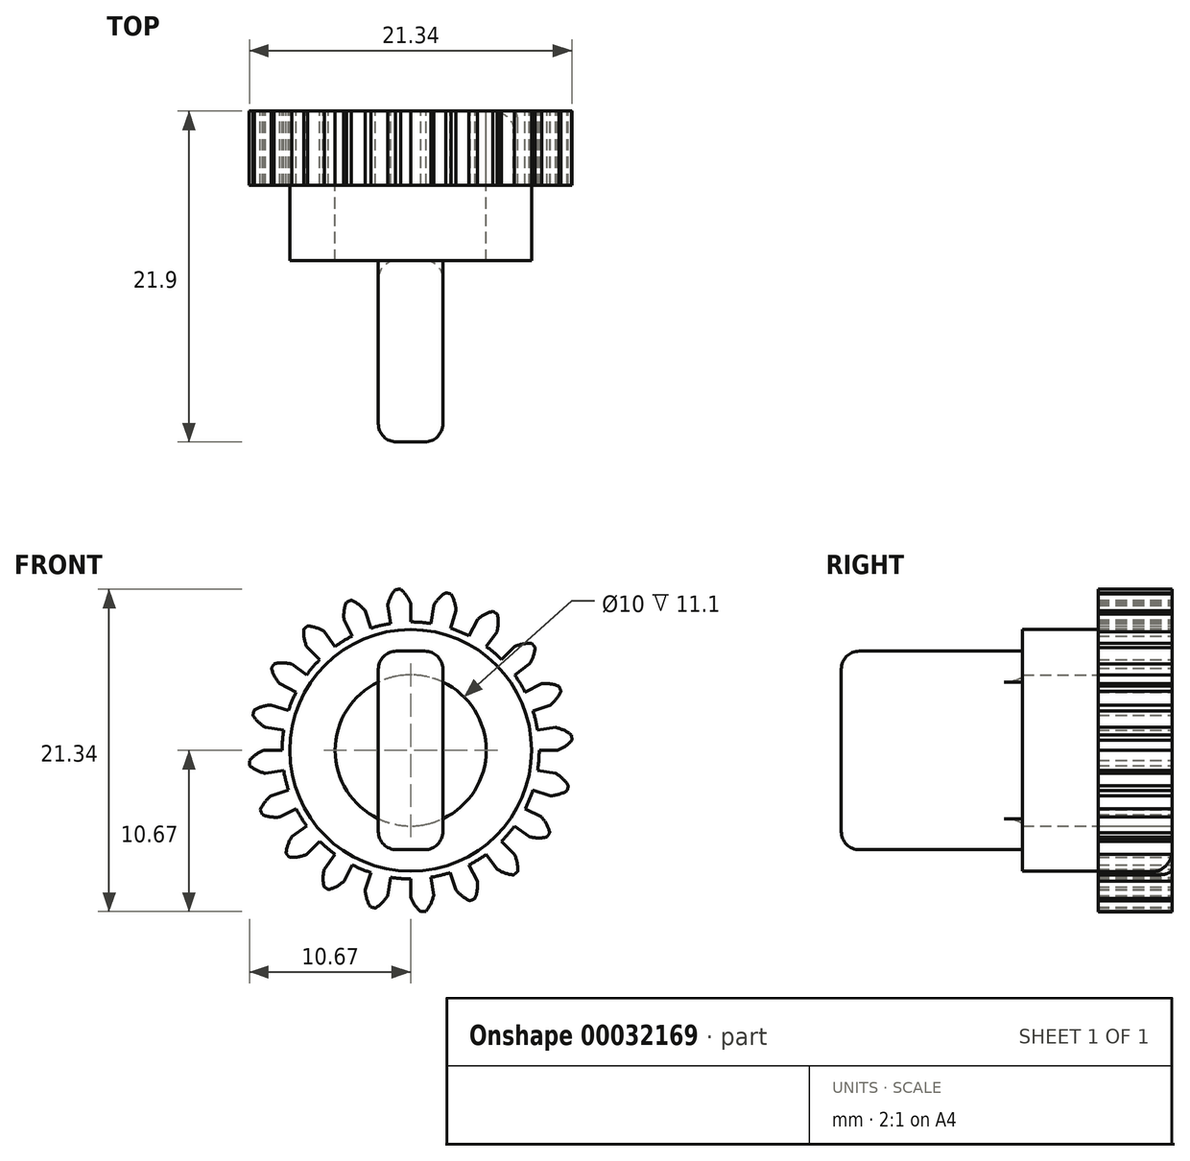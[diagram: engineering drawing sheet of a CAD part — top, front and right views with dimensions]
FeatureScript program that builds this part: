
annotation { "Feature Type Name" : "Feature", "Feature Type Description" : "" }
export const myFeature = defineFeature(function(context is Context, id is Id, definition is map)
    precondition{}
    {
        {
            var Q0;
            Q0=qCreatedBy(makeId("Front.planeOp"),FACE);
            var sketch = newSketch(context, id + "F0", { "sketchPlane" : qUnion([Q0])});
            skCircle(sketch, "E0", {"center": v(0, 0) * mm, "radius": 5 * mm});
            skArc(sketch, "E1", {"start": v(-1.33, 8.4) * mm, "mid": v(0.67, -8.48) * mm, "end": v(0, 8.5) * mm});
            skArc(sketch, "E2", {"start": v(-0.66, 10.67) * mm, "mid": v(-0.84, 10.66) * mm, "end": v(-1.01, 10.65) * mm});
            skArc(sketch, "E3.trimOffspring", {"start": v(0, 9.72) * mm, "mid": v(-0.27, 10.24) * mm, "end": v(-0.66, 10.67) * mm});
            skArc(sketch, "E4.0.MirrorCS", {"start": v(-1.52, 9.6) * mm, "mid": v(-1.33, 10.15) * mm, "end": v(-1.01, 10.65) * mm});
            skPoint(sketch, "E5.trimOffspring.end.orphan", {"position": v(-2.25, 14.23) * mm});
            skPoint(sketch, "E6.trimOffspring.end.orphan", {"position": v(0, 14.4) * mm});
            skLineSegment(sketch, "E7.trimOffspring", {"start": v(-1.33, 8.4) * mm, "end": v(-1.52, 9.6) * mm});
            skLineSegment(sketch, "E8.trimOffspring", {"start": v(0, 8.5) * mm, "end": v(0, 9.72) * mm});
            skSolve(sketch);
        }
        {
            var Q0;
            Q0=makeQuery(id+"F0.imprint","IMPRINT",FACE,{"disambiguationData":[TD([[makeQuery(id+"F0.imprint","IMPRINT",EDGE,{"derivedFrom":sQuery(id+"F0.wireOp",EDGE,"E0")}),-1.0]])]});
            extrude(context, id + "F1", {"entities" : qUnion([Q0]), "depth" : 4.9 * mm});
        }
        {
            var Q0;
            Q0=makeQuery(id+"F1.opExtrude","SWEPT_BODY",BODY,{"disambiguationData":[OSD([sQuery(id+"F0.wireOp",EDGE,"E0"),sQuery(id+"F0.wireOp",EDGE,"E1"),sQuery(id+"F0.wireOp",EDGE,"E2"),sQuery(id+"F0.wireOp",EDGE,"E3.trimOffspring"),sQuery(id+"F0.wireOp",EDGE,"E4.0.MirrorCS"),sQuery(id+"F0.wireOp",EDGE,"E7.trimOffspring"),sQuery(id+"F0.wireOp",EDGE,"E8.trimOffspring")])]});
            var Q1;
            Q1=makeQuery(id+"F1.opExtrude","SWEPT_FACE",FACE,{"disambiguationData":[OSD([sQuery(id+"F0.wireOp",EDGE,"E0")])]});
            circularPattern(context, id + "F2", {"entities" : qUnion([Q0]), "axis" : qUnion([Q1]), "angle" : 18 * degree, "instanceCount" : 20});
        }
        {
            var Q0;
            Q0=makeQuery(id+"F2.opPattern","COPY",BODY,{"derivedFrom":makeQuery(id+"F1.opExtrude","SWEPT_BODY",BODY,{"disambiguationData":[OSD([sQuery(id+"F0.wireOp",EDGE,"E0"),sQuery(id+"F0.wireOp",EDGE,"E1"),sQuery(id+"F0.wireOp",EDGE,"E2"),sQuery(id+"F0.wireOp",EDGE,"E3.trimOffspring"),sQuery(id+"F0.wireOp",EDGE,"E4.0.MirrorCS"),sQuery(id+"F0.wireOp",EDGE,"E7.trimOffspring"),sQuery(id+"F0.wireOp",EDGE,"E8.trimOffspring")])]}),"instanceName":"7"});
            var Q1;
            Q1=makeQuery(id+"F2.opPattern","COPY",BODY,{"derivedFrom":makeQuery(id+"F1.opExtrude","SWEPT_BODY",BODY,{"disambiguationData":[OSD([sQuery(id+"F0.wireOp",EDGE,"E0"),sQuery(id+"F0.wireOp",EDGE,"E1"),sQuery(id+"F0.wireOp",EDGE,"E2"),sQuery(id+"F0.wireOp",EDGE,"E3.trimOffspring"),sQuery(id+"F0.wireOp",EDGE,"E4.0.MirrorCS"),sQuery(id+"F0.wireOp",EDGE,"E7.trimOffspring"),sQuery(id+"F0.wireOp",EDGE,"E8.trimOffspring")])]}),"instanceName":"15"});
            var Q2;
            Q2=makeQuery(id+"F2.opPattern","COPY",BODY,{"derivedFrom":makeQuery(id+"F1.opExtrude","SWEPT_BODY",BODY,{"disambiguationData":[OSD([sQuery(id+"F0.wireOp",EDGE,"E0"),sQuery(id+"F0.wireOp",EDGE,"E1"),sQuery(id+"F0.wireOp",EDGE,"E2"),sQuery(id+"F0.wireOp",EDGE,"E3.trimOffspring"),sQuery(id+"F0.wireOp",EDGE,"E4.0.MirrorCS"),sQuery(id+"F0.wireOp",EDGE,"E7.trimOffspring"),sQuery(id+"F0.wireOp",EDGE,"E8.trimOffspring")])]}),"instanceName":"16"});
            var Q3;
            Q3=makeQuery(id+"F2.opPattern","COPY",BODY,{"derivedFrom":makeQuery(id+"F1.opExtrude","SWEPT_BODY",BODY,{"disambiguationData":[OSD([sQuery(id+"F0.wireOp",EDGE,"E0"),sQuery(id+"F0.wireOp",EDGE,"E1"),sQuery(id+"F0.wireOp",EDGE,"E2"),sQuery(id+"F0.wireOp",EDGE,"E3.trimOffspring"),sQuery(id+"F0.wireOp",EDGE,"E4.0.MirrorCS"),sQuery(id+"F0.wireOp",EDGE,"E7.trimOffspring"),sQuery(id+"F0.wireOp",EDGE,"E8.trimOffspring")])]}),"instanceName":"1"});
            var Q4;
            Q4=makeQuery(id+"F2.opPattern","COPY",BODY,{"derivedFrom":makeQuery(id+"F1.opExtrude","SWEPT_BODY",BODY,{"disambiguationData":[OSD([sQuery(id+"F0.wireOp",EDGE,"E0"),sQuery(id+"F0.wireOp",EDGE,"E1"),sQuery(id+"F0.wireOp",EDGE,"E2"),sQuery(id+"F0.wireOp",EDGE,"E3.trimOffspring"),sQuery(id+"F0.wireOp",EDGE,"E4.0.MirrorCS"),sQuery(id+"F0.wireOp",EDGE,"E7.trimOffspring"),sQuery(id+"F0.wireOp",EDGE,"E8.trimOffspring")])]}),"instanceName":"5"});
            var Q5;
            Q5=makeQuery(id+"F2.opPattern","COPY",BODY,{"derivedFrom":makeQuery(id+"F1.opExtrude","SWEPT_BODY",BODY,{"disambiguationData":[OSD([sQuery(id+"F0.wireOp",EDGE,"E0"),sQuery(id+"F0.wireOp",EDGE,"E1"),sQuery(id+"F0.wireOp",EDGE,"E2"),sQuery(id+"F0.wireOp",EDGE,"E3.trimOffspring"),sQuery(id+"F0.wireOp",EDGE,"E4.0.MirrorCS"),sQuery(id+"F0.wireOp",EDGE,"E7.trimOffspring"),sQuery(id+"F0.wireOp",EDGE,"E8.trimOffspring")])]}),"instanceName":"9"});
            var Q6;
            Q6=makeQuery(id+"F2.opPattern","COPY",BODY,{"derivedFrom":makeQuery(id+"F1.opExtrude","SWEPT_BODY",BODY,{"disambiguationData":[OSD([sQuery(id+"F0.wireOp",EDGE,"E0"),sQuery(id+"F0.wireOp",EDGE,"E1"),sQuery(id+"F0.wireOp",EDGE,"E2"),sQuery(id+"F0.wireOp",EDGE,"E3.trimOffspring"),sQuery(id+"F0.wireOp",EDGE,"E4.0.MirrorCS"),sQuery(id+"F0.wireOp",EDGE,"E7.trimOffspring"),sQuery(id+"F0.wireOp",EDGE,"E8.trimOffspring")])]}),"instanceName":"3"});
            var Q7;
            Q7=makeQuery(id+"F2.opPattern","COPY",BODY,{"derivedFrom":makeQuery(id+"F1.opExtrude","SWEPT_BODY",BODY,{"disambiguationData":[OSD([sQuery(id+"F0.wireOp",EDGE,"E0"),sQuery(id+"F0.wireOp",EDGE,"E1"),sQuery(id+"F0.wireOp",EDGE,"E2"),sQuery(id+"F0.wireOp",EDGE,"E3.trimOffspring"),sQuery(id+"F0.wireOp",EDGE,"E4.0.MirrorCS"),sQuery(id+"F0.wireOp",EDGE,"E7.trimOffspring"),sQuery(id+"F0.wireOp",EDGE,"E8.trimOffspring")])]}),"instanceName":"12"});
            var Q8;
            Q8=makeQuery(id+"F2.opPattern","COPY",BODY,{"derivedFrom":makeQuery(id+"F1.opExtrude","SWEPT_BODY",BODY,{"disambiguationData":[OSD([sQuery(id+"F0.wireOp",EDGE,"E0"),sQuery(id+"F0.wireOp",EDGE,"E1"),sQuery(id+"F0.wireOp",EDGE,"E2"),sQuery(id+"F0.wireOp",EDGE,"E3.trimOffspring"),sQuery(id+"F0.wireOp",EDGE,"E4.0.MirrorCS"),sQuery(id+"F0.wireOp",EDGE,"E7.trimOffspring"),sQuery(id+"F0.wireOp",EDGE,"E8.trimOffspring")])]}),"instanceName":"4"});
            var Q9;
            Q9=makeQuery(id+"F2.opPattern","COPY",BODY,{"derivedFrom":makeQuery(id+"F1.opExtrude","SWEPT_BODY",BODY,{"disambiguationData":[OSD([sQuery(id+"F0.wireOp",EDGE,"E0"),sQuery(id+"F0.wireOp",EDGE,"E1"),sQuery(id+"F0.wireOp",EDGE,"E2"),sQuery(id+"F0.wireOp",EDGE,"E3.trimOffspring"),sQuery(id+"F0.wireOp",EDGE,"E4.0.MirrorCS"),sQuery(id+"F0.wireOp",EDGE,"E7.trimOffspring"),sQuery(id+"F0.wireOp",EDGE,"E8.trimOffspring")])]}),"instanceName":"11"});
            var Q10;
            Q10=makeQuery(id+"F2.opPattern","COPY",BODY,{"derivedFrom":makeQuery(id+"F1.opExtrude","SWEPT_BODY",BODY,{"disambiguationData":[OSD([sQuery(id+"F0.wireOp",EDGE,"E0"),sQuery(id+"F0.wireOp",EDGE,"E1"),sQuery(id+"F0.wireOp",EDGE,"E2"),sQuery(id+"F0.wireOp",EDGE,"E3.trimOffspring"),sQuery(id+"F0.wireOp",EDGE,"E4.0.MirrorCS"),sQuery(id+"F0.wireOp",EDGE,"E7.trimOffspring"),sQuery(id+"F0.wireOp",EDGE,"E8.trimOffspring")])]}),"instanceName":"10"});
            var Q11;
            Q11=makeQuery(id+"F2.opPattern","COPY",BODY,{"derivedFrom":makeQuery(id+"F1.opExtrude","SWEPT_BODY",BODY,{"disambiguationData":[OSD([sQuery(id+"F0.wireOp",EDGE,"E0"),sQuery(id+"F0.wireOp",EDGE,"E1"),sQuery(id+"F0.wireOp",EDGE,"E2"),sQuery(id+"F0.wireOp",EDGE,"E3.trimOffspring"),sQuery(id+"F0.wireOp",EDGE,"E4.0.MirrorCS"),sQuery(id+"F0.wireOp",EDGE,"E7.trimOffspring"),sQuery(id+"F0.wireOp",EDGE,"E8.trimOffspring")])]}),"instanceName":"2"});
            var Q12;
            Q12=makeQuery(id+"F2.opPattern","COPY",BODY,{"derivedFrom":makeQuery(id+"F1.opExtrude","SWEPT_BODY",BODY,{"disambiguationData":[OSD([sQuery(id+"F0.wireOp",EDGE,"E0"),sQuery(id+"F0.wireOp",EDGE,"E1"),sQuery(id+"F0.wireOp",EDGE,"E2"),sQuery(id+"F0.wireOp",EDGE,"E3.trimOffspring"),sQuery(id+"F0.wireOp",EDGE,"E4.0.MirrorCS"),sQuery(id+"F0.wireOp",EDGE,"E7.trimOffspring"),sQuery(id+"F0.wireOp",EDGE,"E8.trimOffspring")])]}),"instanceName":"6"});
            var Q13;
            Q13=makeQuery(id+"F2.opPattern","COPY",BODY,{"derivedFrom":makeQuery(id+"F1.opExtrude","SWEPT_BODY",BODY,{"disambiguationData":[OSD([sQuery(id+"F0.wireOp",EDGE,"E0"),sQuery(id+"F0.wireOp",EDGE,"E1"),sQuery(id+"F0.wireOp",EDGE,"E2"),sQuery(id+"F0.wireOp",EDGE,"E3.trimOffspring"),sQuery(id+"F0.wireOp",EDGE,"E4.0.MirrorCS"),sQuery(id+"F0.wireOp",EDGE,"E7.trimOffspring"),sQuery(id+"F0.wireOp",EDGE,"E8.trimOffspring")])]}),"instanceName":"8"});
            var Q14;
            Q14=makeQuery(id+"F2.opPattern","COPY",BODY,{"derivedFrom":makeQuery(id+"F1.opExtrude","SWEPT_BODY",BODY,{"disambiguationData":[OSD([sQuery(id+"F0.wireOp",EDGE,"E0"),sQuery(id+"F0.wireOp",EDGE,"E1"),sQuery(id+"F0.wireOp",EDGE,"E2"),sQuery(id+"F0.wireOp",EDGE,"E3.trimOffspring"),sQuery(id+"F0.wireOp",EDGE,"E4.0.MirrorCS"),sQuery(id+"F0.wireOp",EDGE,"E7.trimOffspring"),sQuery(id+"F0.wireOp",EDGE,"E8.trimOffspring")])]}),"instanceName":"13"});
            var Q15;
            Q15=makeQuery(id+"F2.opPattern","COPY",BODY,{"derivedFrom":makeQuery(id+"F1.opExtrude","SWEPT_BODY",BODY,{"disambiguationData":[OSD([sQuery(id+"F0.wireOp",EDGE,"E0"),sQuery(id+"F0.wireOp",EDGE,"E1"),sQuery(id+"F0.wireOp",EDGE,"E2"),sQuery(id+"F0.wireOp",EDGE,"E3.trimOffspring"),sQuery(id+"F0.wireOp",EDGE,"E4.0.MirrorCS"),sQuery(id+"F0.wireOp",EDGE,"E7.trimOffspring"),sQuery(id+"F0.wireOp",EDGE,"E8.trimOffspring")])]}),"instanceName":"14"});
            var Q16;
            Q16=makeQuery(id+"F1.opExtrude","SWEPT_BODY",BODY,{"disambiguationData":[OSD([sQuery(id+"F0.wireOp",EDGE,"E0"),sQuery(id+"F0.wireOp",EDGE,"E1"),sQuery(id+"F0.wireOp",EDGE,"E2"),sQuery(id+"F0.wireOp",EDGE,"E3.trimOffspring"),sQuery(id+"F0.wireOp",EDGE,"E4.0.MirrorCS"),sQuery(id+"F0.wireOp",EDGE,"E7.trimOffspring"),sQuery(id+"F0.wireOp",EDGE,"E8.trimOffspring")])]});
            booleanBodies(context, id + "F3", {"operationType" : BooleanOperationType.UNION, "tools" : qUnion([Q0, Q1, Q2, Q3, Q4, Q5, Q6, Q7, Q8, Q9, Q10, Q11, Q12, Q13, Q14, Q15, Q16])});
        }
        {
            var Q0;
            {var subQ0=makeQuery(id+"F1.opExtrude","CAP_FACE",FACE,{"disambiguationData":[OSD([sQuery(id+"F0.wireOp",EDGE,"E0"),sQuery(id+"F0.wireOp",EDGE,"E1"),sQuery(id+"F0.wireOp",EDGE,"E2"),sQuery(id+"F0.wireOp",EDGE,"E3.trimOffspring"),sQuery(id+"F0.wireOp",EDGE,"E4.0.MirrorCS"),sQuery(id+"F0.wireOp",EDGE,"E7.trimOffspring"),sQuery(id+"F0.wireOp",EDGE,"E8.trimOffspring")])],"isStart":false});Q0=makeQuery(id+"F3.opBoolean","MERGE",FACE,{"derivedFrom":[subQ0,makeQuery(id+"F2.opPattern","COPY",FACE,{"derivedFrom":subQ0,"instanceName":"1"}),makeQuery(id+"F2.opPattern","COPY",FACE,{"derivedFrom":subQ0,"instanceName":"2"}),makeQuery(id+"F2.opPattern","COPY",FACE,{"derivedFrom":subQ0,"instanceName":"3"}),makeQuery(id+"F2.opPattern","COPY",FACE,{"derivedFrom":subQ0,"instanceName":"4"}),makeQuery(id+"F2.opPattern","COPY",FACE,{"derivedFrom":subQ0,"instanceName":"5"}),makeQuery(id+"F2.opPattern","COPY",FACE,{"derivedFrom":subQ0,"instanceName":"6"}),makeQuery(id+"F2.opPattern","COPY",FACE,{"derivedFrom":subQ0,"instanceName":"7"}),makeQuery(id+"F2.opPattern","COPY",FACE,{"derivedFrom":subQ0,"instanceName":"8"}),makeQuery(id+"F2.opPattern","COPY",FACE,{"derivedFrom":subQ0,"instanceName":"9"}),makeQuery(id+"F2.opPattern","COPY",FACE,{"derivedFrom":subQ0,"instanceName":"10"}),makeQuery(id+"F2.opPattern","COPY",FACE,{"derivedFrom":subQ0,"instanceName":"11"}),makeQuery(id+"F2.opPattern","COPY",FACE,{"derivedFrom":subQ0,"instanceName":"12"}),makeQuery(id+"F2.opPattern","COPY",FACE,{"derivedFrom":subQ0,"instanceName":"13"}),makeQuery(id+"F2.opPattern","COPY",FACE,{"derivedFrom":subQ0,"instanceName":"14"}),makeQuery(id+"F2.opPattern","COPY",FACE,{"derivedFrom":subQ0,"instanceName":"15"}),makeQuery(id+"F2.opPattern","COPY",FACE,{"derivedFrom":subQ0,"instanceName":"16"})]});}
            var sketch = newSketch(context, id + "F4", { "sketchPlane" : qUnion([Q0])});
            skPoint(sketch, "E9.rect.middle", {"position": v(0, 0) * mm});
            skCircle(sketch, "E10", {"center": v(0, 0) * mm, "radius": 8 * mm});
            skSolve(sketch);
        }
        {
            var Q0;
            {var subQ8=sQuery(id+"F4.wireOp",EDGE,"E9.rect.bottom");Q0=makeQuery(id+"F4.imprint","IMPRINT",FACE,{"disambiguationData":[TD([[makeQuery(id+"F4.imprint","IMPRINT",EDGE,{"derivedFrom":subQ8}),-1.0]])]});}
            var Q1;
            Q1=makeQuery(id+"F4.imprint","IMPRINT",FACE,{"disambiguationData":[TD([[makeQuery(id+"F4.imprint","IMPRINT",EDGE,{"derivedFrom":sQuery(id+"F4.wireOp",EDGE,"E10")}),1.0]])]});
            extrude(context, id + "F5", {"entities" : qUnion([Q0, Q1]), "operationType" : NewBodyOperationType.ADD, "depth" : 5 * mm});
        }
        {
            var Q0;
            Q0=makeQuery(id+"F5.opExtrude","CAP_FACE",FACE,{"disambiguationData":[OSD([sQuery(id+"F0.wireOp",EDGE,"E0"),sQuery(id+"F4.wireOp",EDGE,"E10")])],"isStart":false});
            var sketch = newSketch(context, id + "F6", { "sketchPlane" : qUnion([Q0])});
            skLineSegment(sketch, "E11.rect.bottom", {"start": v(2.14, 6.57) * mm, "end": v(-2.14, 6.57) * mm});
            skLineSegment(sketch, "E11.rect.top", {"start": v(2.14, -6.57) * mm, "end": v(-2.14, -6.57) * mm});
            skLineSegment(sketch, "E11.rect.left", {"start": v(2.14, 6.57) * mm, "end": v(2.14, -6.57) * mm});
            skLineSegment(sketch, "E11.rect.right", {"start": v(-2.14, 6.57) * mm, "end": v(-2.14, -6.57) * mm});
            skPoint(sketch, "E11.rect.middle", {"position": v(0, 0) * mm});
            skSolve(sketch);
        }
        {
            var Q0;
            {var subQ5=sQuery(id+"F6.wireOp",EDGE,"E11.rect.top");Q0=makeQuery(id+"F6.imprint","IMPRINT",FACE,{"disambiguationData":[TD([[makeQuery(id+"F6.imprint","IMPRINT",EDGE,{"derivedFrom":subQ5}),-1.0]])]});}
            var Q1;
            {var subQ0=makeQuery(id+"F5.opExtrude","CAP_EDGE",EDGE,{"disambiguationData":[OSD([sQuery(id+"F0.wireOp",EDGE,"E0")])],"isStart":false});var subQ3=sQuery(id+"F6.wireOp",EDGE,"E11.rect.left");var subQ6=makeQuery(id+"F6.imprint","INTERSECT",VERTEX,{"disambiguationData":[OD(0.0)],"derivedFrom":[subQ0,subQ3]});Q1=makeQuery(id+"F6.imprint","IMPRINT",FACE,{"disambiguationData":[TD([[makeQuery(id+"F6.imprint","IMPRINT",EDGE,{"disambiguationData":[TD([[subQ6,-1.0]])],"derivedFrom":subQ3}),-1.0]])]});}
            var Q2;
            {var subQ5=sQuery(id+"F6.wireOp",EDGE,"E11.rect.bottom");Q2=makeQuery(id+"F6.imprint","IMPRINT",FACE,{"disambiguationData":[TD([[makeQuery(id+"F6.imprint","IMPRINT",EDGE,{"derivedFrom":subQ5}),1.0]])]});}
            extrude(context, id + "F7", {"entities" : qUnion([Q0, Q1, Q2]), "operationType" : NewBodyOperationType.ADD, "depth" : 12 * mm});
        }
        {
            var Q0;
            Q0=makeQuery(id+"F7.opExtrude","SWEPT_EDGE",EDGE,{"disambiguationData":[OSD([sQuery(id+"F6.wireOp",EDGE,"E11.rect.bottom"),sQuery(id+"F6.wireOp",EDGE,"E11.rect.right")])]});
            var Q1;
            {var subQ0=sQuery(id+"F6.wireOp",EDGE,"E11.rect.right");var subQ1=sQuery(id+"F6.wireOp",EDGE,"E11.rect.bottom");var subQ2=sQuery(id+"F0.wireOp",EDGE,"E0");var subQ3=makeQuery(id+"F1.opExtrude","SWEPT_FACE",FACE,{"disambiguationData":[OSD([subQ2])]});Q1=makeQuery(id+"F7.boolean.opBoolean","SPLIT",EDGE,{"disambiguationData":[TD([makeQuery(id+"F2.opPattern","COPY",FACE,{"derivedFrom":subQ3,"instanceName":"7"}),makeQuery(id+"F2.opPattern","COPY",FACE,{"derivedFrom":subQ3,"instanceName":"17"}),makeQuery(id+"F2.opPattern","COPY",FACE,{"derivedFrom":subQ3,"instanceName":"18"}),makeQuery(id+"F2.opPattern","COPY",FACE,{"derivedFrom":subQ3,"instanceName":"19"}),makeQuery(id+"F5.opExtrude","CAP_FACE",FACE,{"disambiguationData":[OSD([subQ2,sQuery(id+"F4.wireOp",EDGE,"E10")])],"isStart":false}),makeQuery(id+"F5.opExtrude","SWEPT_FACE",FACE,{"disambiguationData":[OSD([subQ2])]}),makeQuery(id+"F7.opExtrude","SWEPT_FACE",FACE,{"disambiguationData":[OSD([subQ1])]}),makeQuery(id+"F7.opExtrude","CAP_FACE",FACE,{"disambiguationData":[OSD([subQ1,sQuery(id+"F6.wireOp",EDGE,"E11.rect.top"),sQuery(id+"F6.wireOp",EDGE,"E11.rect.left"),subQ0])],"isStart":true}),makeQuery(id+"F7.opExtrude","SWEPT_FACE",FACE,{"disambiguationData":[OSD([subQ0])]})])],"derivedFrom":makeQuery(id+"F7.opExtrude","CAP_EDGE",EDGE,{"disambiguationData":[OSD([subQ0])],"isStart":true})});}
            var Q2;
            {var subQ0=sQuery(id+"F6.wireOp",EDGE,"E11.rect.right");var subQ1=sQuery(id+"F6.wireOp",EDGE,"E11.rect.top");var subQ2=sQuery(id+"F0.wireOp",EDGE,"E0");var subQ3=makeQuery(id+"F1.opExtrude","SWEPT_FACE",FACE,{"disambiguationData":[OSD([subQ2])]});Q2=makeQuery(id+"F7.boolean.opBoolean","SPLIT",EDGE,{"disambiguationData":[TD([makeQuery(id+"F2.opPattern","COPY",FACE,{"derivedFrom":subQ3,"instanceName":"7"}),makeQuery(id+"F2.opPattern","COPY",FACE,{"derivedFrom":subQ3,"instanceName":"17"}),makeQuery(id+"F2.opPattern","COPY",FACE,{"derivedFrom":subQ3,"instanceName":"18"}),makeQuery(id+"F2.opPattern","COPY",FACE,{"derivedFrom":subQ3,"instanceName":"19"}),makeQuery(id+"F5.opExtrude","CAP_FACE",FACE,{"disambiguationData":[OSD([subQ2,sQuery(id+"F4.wireOp",EDGE,"E10")])],"isStart":false}),makeQuery(id+"F5.opExtrude","SWEPT_FACE",FACE,{"disambiguationData":[OSD([subQ2])]}),makeQuery(id+"F7.opExtrude","CAP_FACE",FACE,{"disambiguationData":[OSD([sQuery(id+"F6.wireOp",EDGE,"E11.rect.bottom"),subQ1,sQuery(id+"F6.wireOp",EDGE,"E11.rect.left"),subQ0])],"isStart":true}),makeQuery(id+"F7.opExtrude","SWEPT_FACE",FACE,{"disambiguationData":[OSD([subQ1])]}),makeQuery(id+"F7.opExtrude","SWEPT_FACE",FACE,{"disambiguationData":[OSD([subQ0])]})])],"derivedFrom":makeQuery(id+"F7.opExtrude","CAP_EDGE",EDGE,{"disambiguationData":[OSD([subQ0])],"isStart":true})});}
            var Q3;
            Q3=makeQuery(id+"F7.opExtrude","CAP_EDGE",EDGE,{"disambiguationData":[OSD([sQuery(id+"F6.wireOp",EDGE,"E11.rect.top")])],"isStart":true});
            var Q4;
            {var subQ0=sQuery(id+"F6.wireOp",EDGE,"E11.rect.left");var subQ1=sQuery(id+"F6.wireOp",EDGE,"E11.rect.bottom");var subQ2=sQuery(id+"F0.wireOp",EDGE,"E0");var subQ3=makeQuery(id+"F1.opExtrude","SWEPT_FACE",FACE,{"disambiguationData":[OSD([subQ2])]});Q4=makeQuery(id+"F7.boolean.opBoolean","SPLIT",EDGE,{"disambiguationData":[TD([makeQuery(id+"F2.opPattern","COPY",FACE,{"derivedFrom":subQ3,"instanceName":"7"}),makeQuery(id+"F2.opPattern","COPY",FACE,{"derivedFrom":subQ3,"instanceName":"17"}),makeQuery(id+"F2.opPattern","COPY",FACE,{"derivedFrom":subQ3,"instanceName":"18"}),makeQuery(id+"F2.opPattern","COPY",FACE,{"derivedFrom":subQ3,"instanceName":"19"}),makeQuery(id+"F5.opExtrude","CAP_FACE",FACE,{"disambiguationData":[OSD([subQ2,sQuery(id+"F4.wireOp",EDGE,"E10")])],"isStart":false}),makeQuery(id+"F5.opExtrude","SWEPT_FACE",FACE,{"disambiguationData":[OSD([subQ2])]}),makeQuery(id+"F7.opExtrude","SWEPT_FACE",FACE,{"disambiguationData":[OSD([subQ1])]}),makeQuery(id+"F7.opExtrude","CAP_FACE",FACE,{"disambiguationData":[OSD([subQ1,sQuery(id+"F6.wireOp",EDGE,"E11.rect.top"),subQ0,sQuery(id+"F6.wireOp",EDGE,"E11.rect.right")])],"isStart":true}),makeQuery(id+"F7.opExtrude","SWEPT_FACE",FACE,{"disambiguationData":[OSD([subQ0])]})])],"derivedFrom":makeQuery(id+"F7.opExtrude","CAP_EDGE",EDGE,{"disambiguationData":[OSD([subQ0])],"isStart":true})});}
            var Q5;
            Q5=makeQuery(id+"F7.opExtrude","SWEPT_EDGE",EDGE,{"disambiguationData":[OSD([sQuery(id+"F6.wireOp",EDGE,"E11.rect.bottom"),sQuery(id+"F6.wireOp",EDGE,"E11.rect.left")])]});
            var Q6;
            Q6=makeQuery(id+"F7.opExtrude","SWEPT_EDGE",EDGE,{"disambiguationData":[OSD([sQuery(id+"F6.wireOp",EDGE,"E11.rect.top"),sQuery(id+"F6.wireOp",EDGE,"E11.rect.left")])]});
            var Q7;
            Q7=makeQuery(id+"F7.opExtrude","SWEPT_EDGE",EDGE,{"disambiguationData":[OSD([sQuery(id+"F6.wireOp",EDGE,"E11.rect.top"),sQuery(id+"F6.wireOp",EDGE,"E11.rect.right")])]});
            var Q8;
            Q8=makeQuery(id+"F7.opExtrude","CAP_EDGE",EDGE,{"disambiguationData":[OSD([sQuery(id+"F6.wireOp",EDGE,"E11.rect.right")])],"isStart":false});
            var Q9;
            Q9=makeQuery(id+"F7.opExtrude","CAP_EDGE",EDGE,{"disambiguationData":[OSD([sQuery(id+"F6.wireOp",EDGE,"E11.rect.left")])],"isStart":false});
            var Q10;
            Q10=makeQuery(id+"F7.opExtrude","CAP_EDGE",EDGE,{"disambiguationData":[OSD([sQuery(id+"F6.wireOp",EDGE,"E11.rect.top")])],"isStart":false});
            var Q11;
            Q11=makeQuery(id+"F7.opExtrude","CAP_EDGE",EDGE,{"disambiguationData":[OSD([sQuery(id+"F6.wireOp",EDGE,"E11.rect.bottom")])],"isStart":false});
            var Q12;
            Q12=makeQuery(id+"F2.opPattern","COPY",EDGE,{"derivedFrom":makeQuery(id+"F1.opExtrude","CAP_EDGE",EDGE,{"disambiguationData":[OSD([sQuery(id+"F0.wireOp",EDGE,"E2")])],"isStart":true}),"instanceName":"12"});
            fillet(context, id + "F8", {"entities" : qUnion([Q0, Q1, Q2, Q3, Q4, Q5, Q6, Q7, Q8, Q9, Q10, Q11, Q12]), "radius" : 1.2 * mm, "tangentPropagation" : true, "allowEdgeOverflow" : false});
        }
    });
